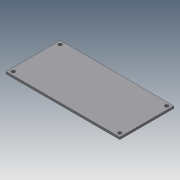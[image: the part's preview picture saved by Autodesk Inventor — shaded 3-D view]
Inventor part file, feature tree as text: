
AUTODESK INVENTOR PART (.ipt)
format: ipt  version: 2014 SP1 (Build 180222100, 222)  size: 84,480 bytes
history: native  units: in
note: dims shown in document units (in); Inventor stores cm internally (conversion verified against a paired STEP export)
features: extrude x1, sketch x1
ambient origin geometry x8: Origin, YZ Plane, XZ Plane, XY Plane, X Axis, Y Axis, Z Axis, Center Point
bodies: Solid1 (feature_tree)
feature tree (2):
  extrude  "Extrusion1"  Depth=1.4961in
  sketch  "Sketch1"  dims[d0=3.1496in d1=1.4961in d2=1.5748in d3=0.748in d4=2.9528in d5=1.2992in d6=0.0984in d7=0.0984in d8=0.0984in d9=0.0625in d10=0.0in]
